# Revit family: Sanitary_Accessories_Svedholm_Slits-table-stand
name_source: partatom
category: Furniture
revit_build: Autodesk Revit 2018 (Build: 20190510_1515(x64)
units: mm (PartAtom-declared; Revit-internal decimal feet)

## family parameters
Always vertical = No
Cut with Voids When Loaded = No
OmniClass Number = 23.21.11.00
OmniClass Title = Commercial Furniture
Room Calculation Point = No
Shared = No
Work Plane-Based = Yes

## types (1)
- ART - (410.600.072)
    BIMobject category = Accessories
    BIMobject category code = sanitary-accessories1
    BIMobject main category = Sanitary
    BIMobject main category code = sanitary
    Brand url = https://www.svedholm.se
    Default Elevation = 1219.2 mm  [stored 4 ft]
    Description = Table stand made of powder coated steel.
    Edition number = 1
    IFC Classification = Object
    Manufacturer = Svedholm
    Manufacturer name = Svedholm
    Model = Slits table stand
    OmniClass Code = 23-21 11 00
    OmniClass Description = Commercial Furniture
    Product Guid = 02fdb585-377b-49e5-b36d-4f9e56db1c20
    Product SKU = Slits-table-stand
    Product data url = https://bimobject.com
    Product family = Slits
    Product group = Stand
    Product name = Slits table stand
    Product url = https://www.svedholm.se
    QR code = http://bimobject.com
    URL = https://www.svedholm.se
    Uniclass 2015 Code = Zz_30_60
    Uniclass 2015 Name = Objects

note: [stored X ft] marks values corroborated as IEEE doubles in the binary element streams (Revit-internal decimal feet)

## geometry (parser evidence)
native form markers: Sweep x3
no freeform markers — native parametric forms only
